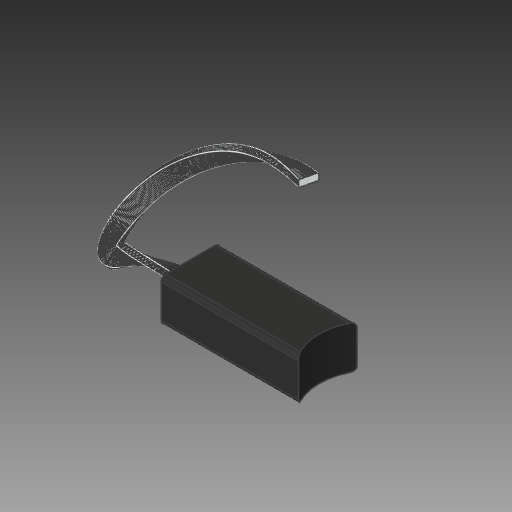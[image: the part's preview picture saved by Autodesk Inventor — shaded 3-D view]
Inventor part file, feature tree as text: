
AUTODESK INVENTOR PART (.ipt)
format: ipt  version: 2018 (Build 220112000, 112)  size: 609,792 bytes
history: native  units: mm
features: other x1, sweep x1
ambient origin geometry x8: Origin, YZ Plane, XZ Plane, XY Plane, X Axis, Y Axis, Z Axis, Center Point
bodies: Body1 (feature_tree)
feature tree (2):
  other  "ソリッド1"
  sweep  "Sweep1"
